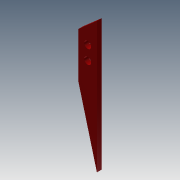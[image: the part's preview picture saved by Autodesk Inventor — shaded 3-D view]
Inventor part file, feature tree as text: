
AUTODESK INVENTOR PART (.ipt)
format: ipt  version: 2013 (Build 170138000, 138)  size: 82,432 bytes
history: native  units: mm
features: extrude x1, sketch x1
ambient origin geometry x8: Origin, YZ Plane, XZ Plane, XY Plane, X Axis, Y Axis, Z Axis, Center Point
bodies: Solid1 (feature_tree)
feature tree (2):
  extrude  "Extrusion1"  Depth=10.0mm
  sketch  "Sketch1"  dims[d2=27.0mm d9=10.0mm d10=3.0mm d11=6.0mm d12=3.0mm d13=20.0mm d14=2.0mm d15=0.0mm]
